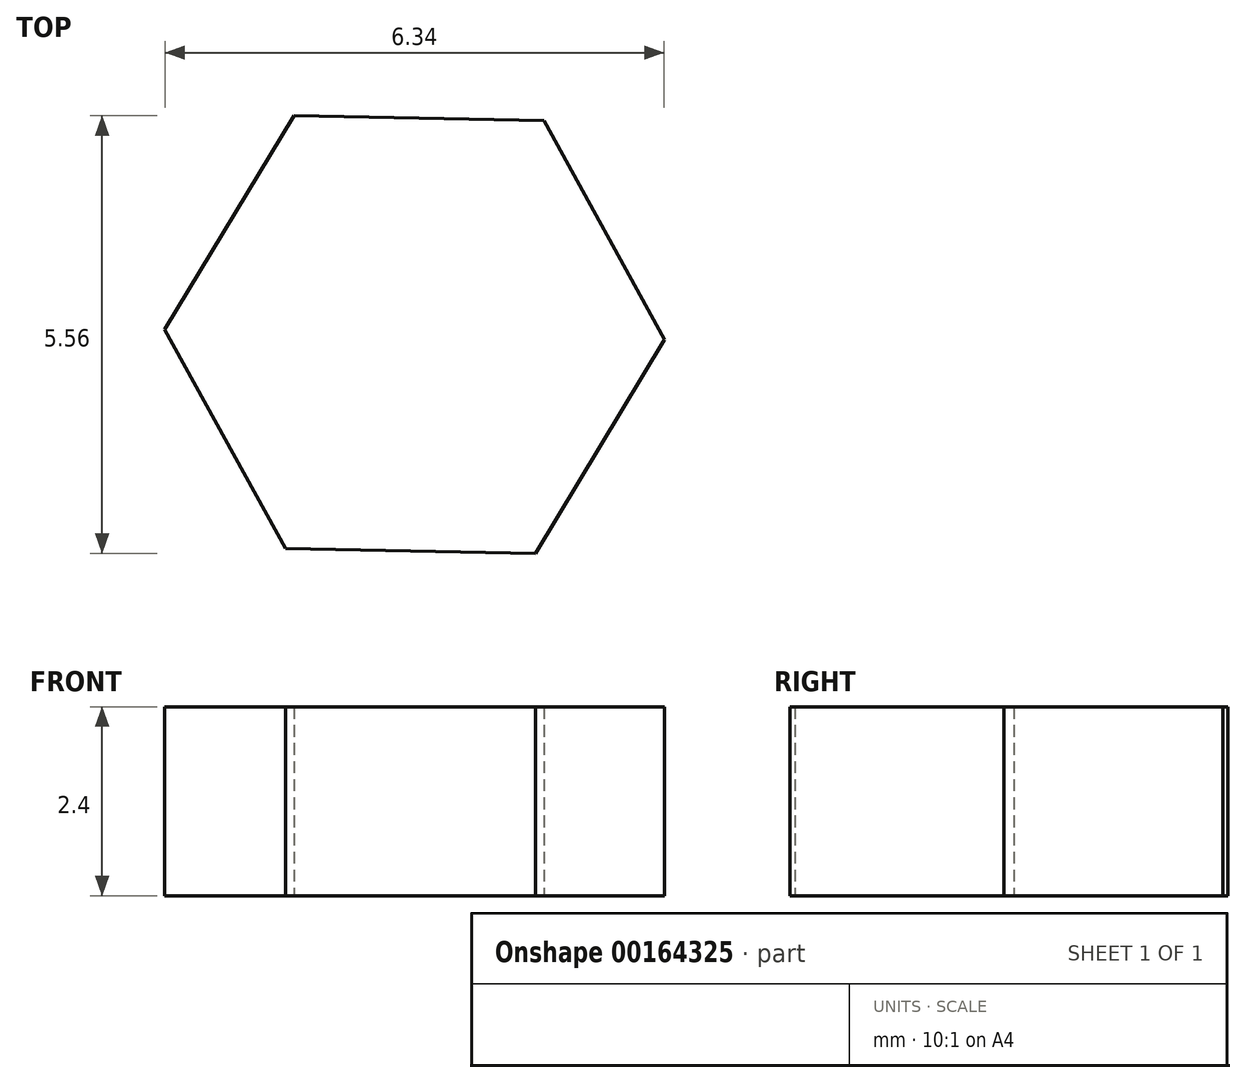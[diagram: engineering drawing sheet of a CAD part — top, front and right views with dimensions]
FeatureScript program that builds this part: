
annotation { "Feature Type Name" : "Feature", "Feature Type Description" : "" }
export const myFeature = defineFeature(function(context is Context, id is Id, definition is map)
    precondition{}
    {
        {
            var Q0;
            Q0=qCreatedBy(makeId("Top.planeOp"),FACE);
            var sketch = newSketch(context, id + "F0", { "sketchPlane" : qUnion([Q0])});
            skCircle(sketch, "E0.cCircle", {"center": v(0, 0) * mm, "radius": 2.75 * mm, "construction": true});
            skLineSegment(sketch, "E0.0", {"start": v(3.17, -0.06) * mm, "end": v(1.53, -2.78) * mm});
            skLineSegment(sketch, "E0.1", {"start": v(1.53, -2.78) * mm, "end": v(-1.64, -2.72) * mm});
            skLineSegment(sketch, "E0.2", {"start": v(-1.64, -2.72) * mm, "end": v(-3.17, 0.06) * mm});
            skLineSegment(sketch, "E0.3", {"start": v(-3.17, 0.06) * mm, "end": v(-1.53, 2.78) * mm});
            skLineSegment(sketch, "E0.4", {"start": v(-1.53, 2.78) * mm, "end": v(1.64, 2.72) * mm});
            skLineSegment(sketch, "E0.5", {"start": v(1.64, 2.72) * mm, "end": v(3.17, -0.06) * mm});
            skPoint(sketch, "E0.0.midPoint", {"position": v(2.35, -1.42) * mm});
            skSolve(sketch);
        }
        {
            var Q0;
            Q0=makeQuery(id+"F0.imprint","IMPRINT",FACE,{"disambiguationData":[TD([[makeQuery(id+"F0.imprint","IMPRINT",EDGE,{"derivedFrom":sQuery(id+"F0.wireOp",EDGE,"E0.0")}),-1.0]])]});
            extrude(context, id + "F1", {"entities" : qUnion([Q0]), "depth" : 2.4 * mm});
        }
    });
